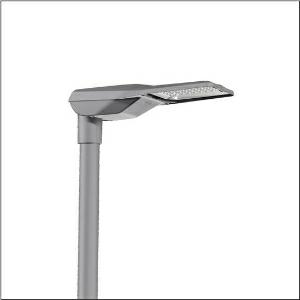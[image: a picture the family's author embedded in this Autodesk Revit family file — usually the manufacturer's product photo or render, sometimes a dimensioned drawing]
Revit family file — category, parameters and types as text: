
# Revit family: streetlight_sl_21_iq_mini___stw1_0a_5xe2e31d08hb_6dd6
name_source: partatom
category: Lighting Fixtures
units: mm (PartAtom-declared; Revit-internal decimal feet)

## family parameters
Cut with Voids When Loaded = No
Host = Face
Light Source = No
Part Type = Normal
Room Calculation Point = No
Round Connector Dimension = Use Diameter
Shared = No

## types (1)
- --- (1 x LED, 9450 lm, 70.9 W, 3000K)
    Apparent Load = 71 VA
    CIE Flux Codes = 38 75 98 100 100
    Color Rendering = 70
    Color Temperature = 3000K
    Default Elevation = 1800 mm
    Description = Streetlight SL 21 mini, mast luminaire, primary light control with lens, of PMMA, primary optical cover: cover, of toughened safety glass, transparent, light distribution: STW1.0a, light emission: direct distribution, primary light characteristic: asymmetric, installation type: post-top, side-entry, LED, High Power LED, rated luminous flux: 9.450lm, luminous efficacy: 133lm/W, light colour: 730, colour temperature: 3000K, control gear: ECG iQ, control: Auto-Match, Temp-Guard, Lumen-Switch, Night-Set, Smart-Wire, Light-Fading, Desk-Remote (wireless, voltage-free reading and setting of iQ features in the workshop via application-optimized NFC function/RFID function), optimised constant luminous flux control (CLO 2.0), mains connection: 220..240V, AC, 50/60Hz, start of lifetime: 71W, end of lifetime: 75W, reduction: 31W, luminaire housing, of diecast aluminium, powder-coated, Siteco® metallic grey (DB 702S), corrosivity category C5 according to DIN EN ISO 12944, length: 628mm, width: 235mm, height: 110mm, spigot size: 60/76mm (post-top) and 42/60/76mm (side-entry), mast flange for spigot size: 42mm: 5XC10008XM4, 60mm: 5XC10008XM2, 76/60mm: 5XC10108XM1, protection rating (complete): IP66, insulation class (complete): insulation class II (safety insulation), certification: CE, ENEC, VDE, impact resistance: IK09, permissible operating ambient temperature for outdoor applications: -40..+50°C, standard-compliant lighting for roads and squares, packaging unit: 1 piece

Light Distribution: STW1.0a
    Height = 110 mm
    Lamp = 1 x LED
    Lamp Light Flux = 9450 lm
    Lamp Power = 70.9 W
    Lamp count = 1
    Length = 625 mm
    Luminous efficacy = 133 lm/W
    Manufacturer = Siteco
    ModVariant = No
    Model = 5XE2E31D08HB
    Number of Poles = 1
    OnlyDefault = Yes
    Power Factor = 1
    Product Name = Streetlight SL 21 iQ mini | STW1.0a
    Product group = mast luminaire | pylon top
    ProductGroupID = 6100
    Protection Class = Protection class II
    Protection Degree = IP 66
    RLX_Detail_Level = 1
    RlxData = <blob elided: 92069 chars, md5=377779ea>
    Socket = socket
    Standby Power = 0 W
    System Light Flux = 9450 lm
    System Power = 71 W
    Type Comments = factory setting: luminous flux: 100 % | dim-lin: 254 | 711 mA
    Type Image = l_1003519.jpg
    URL = http://relux.com
    VarID = @adj_069113
    Voltage = 0 V
    Weight = 0.00 kg
    Width = 234 mm

## geometry (parser evidence)
native form markers: Blend x4, Sweep x11
no freeform markers — native parametric forms only
